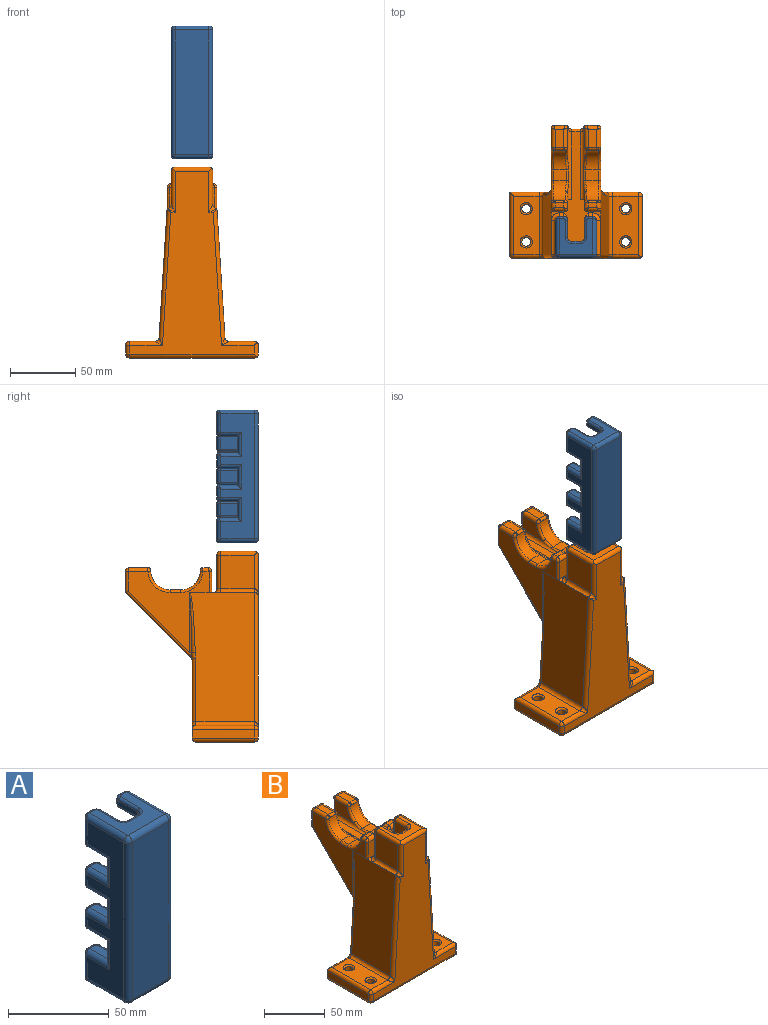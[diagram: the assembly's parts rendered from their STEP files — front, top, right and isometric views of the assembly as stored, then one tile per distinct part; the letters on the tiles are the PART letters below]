
ASSEMBLY  parts=2 mates=1
PART A: 197 faces, bbox 31.8x31.8x101.6 mm
  f0: plane 13.05x3.15mm, normal (-1,0,0), area 41.1mm2, adj f21,f33,f89,f134
  f1: plane 13.05x9.5mm, normal (-1,0,0), area 124mm2, adj f22,f33,f85,f98
  f2: plane 13.05x9.5mm, normal (-1,0,0), area 124mm2, adj f23,f33,f94,f107
  f3: plane 13.05x9.5mm, normal (-1,0,0), area 124mm2, adj f24,f33,f103,f116
  f4: plane 15.85x13.05mm, normal (1,0,0), area 206.8mm2, adj f31,f34,f62,f130
  f5: plane 13.05x9.1mm, normal (1,0,0), area 118.8mm2, adj f13,f34,f71,f76
  f6: plane 16.65x13.05mm, normal (1,0,0), area 217.3mm2, adj f14,f34,f80,f121
  f7: plane 9.1x3.53mm, normal (0,1,0), area 32.1mm2, adj f12,f56,f65,f194
  f8: plane 9.1x3.53mm, normal (0,1,0), area 32.1mm2, adj f13,f73,f74,f187
  f9: plane 16.65x3.53mm, normal (0,1,0), area 58.7mm2, adj f14,f82,f119,f140
  f10: plane 13.05x9.1mm, normal (1,0,0), area 118.8mm2, adj f12,f34,f59,f67
  f11: plane 95.6x25.75mm, normal (-1,0,0), area 1571.1mm2, adj f137,f139,f140,f145,f146,f151,f152,f184
  f12: cylinder r=3mm len=9.1mm, axis (0,0,1), area 42.9mm2, adj f7,f10,f57,f66
  f13: cylinder r=3mm len=9.1mm, axis (0,0,1), area 42.9mm2, adj f5,f8,f72,f75
  f14: cylinder r=3mm len=16.65mm, axis (0,0,1), area 78.5mm2, adj f6,f9,f81,f120
  f15: plane 3.53x3.15mm, normal (0,1,0), area 11.1mm2, adj f21,f91,f136,f162
  f16: plane 9.5x3.53mm, normal (0,1,0), area 33.5mm2, adj f22,f83,f100,f182
  f17: plane 9.5x3.53mm, normal (0,1,0), area 33.5mm2, adj f23,f92,f109,f174
  f18: plane 9.5x3.53mm, normal (0,1,0), area 33.5mm2, adj f24,f101,f118,f168
  f19: plane 95.6x25.75mm, normal (1,0,0), area 1274.2mm2, adj f141,f147,f154,f158,f160,f162,f164,f165
  f20: plane 13.05x3.15mm, normal (-1,0,0), area 41.1mm2, adj f32,f33,f112,f125
  f21: cylinder r=3mm len=3.15mm, axis (0,0,-1), area 14.8mm2, adj f0,f15,f90,f135
  f22: cylinder r=3mm len=9.5mm, axis (0,0,-1), area 44.8mm2, adj f1,f16,f84,f99
  f23: cylinder r=3mm len=9.5mm, axis (0,0,-1), area 44.8mm2, adj f2,f17,f93,f108
  f24: cylinder r=3mm len=9.5mm, axis (0,0,-1), area 44.8mm2, adj f3,f18,f102,f117
  f25: plane 15.85x3.53mm, normal (0,1,0), area 55.9mm2, adj f31,f64,f128,f145
  f26: plane 95.6x25.75mm, normal (0,-1,0), area 2461.7mm2, adj f152,f153,f157,f158
  f27: plane 3.53x3.15mm, normal (0,1,0), area 11.1mm2, adj f32,f110,f127,f147
  f28: plane 98.4x6.7mm, normal (0,1,0), area 659.3mm2, adj f33,f34,f123,f132
  f29: plane 27.15x25.75mm, normal (0,0,1), area 404.5mm2, adj f119,f120,f121,f122,f123,f124,f125,f126
  f30: plane 27.15x25.75mm, normal (0,0,-1), area 404.5mm2, adj f128,f129,f130,f131,f132,f133,f134,f135
  f31: cylinder r=3mm len=15.85mm, axis (0,0,1), area 74.7mm2, adj f4,f25,f63,f129
  f32: cylinder r=3mm len=3.15mm, axis (0,0,-1), area 14.8mm2, adj f20,f27,f111,f126
  f33: cylinder r=3mm len=98.4mm, axis (0,0,-1), area 403.6mm2, adj f0,f1,f2,f3,f20,f28,f86,f87
  f34: cylinder r=3mm len=98.4mm, axis (0,0,1), area 418.6mm2, adj f4,f5,f6,f10,f28,f58,f60,f61
  f35: plane 12.73x5.15mm, normal (0,1,0), area 65.4mm2, adj f36,f37,f112,f114,f116,f165
  f36: plane 14.28x4.93mm, normal (0,0,1), area 69.9mm2, adj f35,f116,f117,f118,f166
  f37: plane 14.28x4.93mm, normal (0,0,-1), area 69.9mm2, adj f35,f110,f111,f112,f141
  f38: plane 12.73x5.15mm, normal (0,1,0), area 65.4mm2, adj f39,f40,f103,f105,f107,f171
  f39: plane 14.28x4.93mm, normal (0,0,1), area 69.9mm2, adj f38,f107,f108,f109,f172
  f40: plane 14.28x4.93mm, normal (0,0,-1), area 69.9mm2, adj f38,f101,f102,f103,f170
  f41: plane 12.73x5.15mm, normal (0,1,0), area 65.4mm2, adj f42,f43,f94,f96,f98,f177
  f42: plane 14.28x4.93mm, normal (0,0,1), area 69.9mm2, adj f41,f98,f99,f100,f178
  f43: plane 14.28x4.93mm, normal (0,0,-1), area 69.9mm2, adj f41,f92,f93,f94,f176
  f44: plane 12.73x5.15mm, normal (0,1,0), area 65.4mm2, adj f45,f46,f85,f87,f89,f179
  f45: plane 14.28x4.93mm, normal (0,0,1), area 69.9mm2, adj f44,f89,f90,f91,f164
  f46: plane 14.28x4.93mm, normal (0,0,-1), area 69.9mm2, adj f44,f83,f84,f85,f181
  f47: plane 12.73x5.15mm, normal (0,1,0), area 65.4mm2, adj f48,f49,f76,f78,f80,f184
  f48: plane 14.28x4.93mm, normal (0,0,-1), area 69.9mm2, adj f47,f80,f81,f82,f137
  f49: plane 14.28x4.93mm, normal (0,0,1), area 69.9mm2, adj f47,f74,f75,f76,f185
  f50: plane 12.73x5.15mm, normal (0,1,0), area 65.4mm2, adj f51,f52,f67,f69,f71,f190
  f51: plane 14.28x4.93mm, normal (0,0,-1), area 69.9mm2, adj f50,f71,f72,f73,f189
  f52: plane 14.28x4.93mm, normal (0,0,1), area 69.9mm2, adj f50,f65,f66,f67,f191
  f53: plane 12.73x5.15mm, normal (0,1,0), area 65.4mm2, adj f54,f55,f59,f61,f62,f193
  f54: plane 14.28x4.93mm, normal (0,0,1), area 69.9mm2, adj f53,f62,f63,f64,f139
  f55: plane 14.28x4.93mm, normal (0,0,-1), area 69.9mm2, adj f53,f56,f57,f59,f195
  f56: cylinder r=1.6mm len=3.53mm, axis (-1,0,0), area 8.9mm2, adj f7,f55,f57,f196
  f57: torus R=1.4mm, axis (0,0,-1), area 9.5mm2, adj f12,f55,f56,f59
  f58: torus R=4.6mm, axis (0,0,-1), area 0.6mm2, adj f34,f59,f61
  f59: cylinder r=1.6mm len=13.05mm, axis (0,1,0), area 32.7mm2, adj f10,f53,f55,f57,f58,f61
  f60: torus R=4.6mm, axis (0,0,-1), area 0.6mm2, adj f34,f61,f62
  f61: cylinder r=1.6mm len=15.9mm, axis (0,0,1), area 28mm2, adj f34,f53,f58,f59,f60,f62
  f62: cylinder r=1.6mm len=13.05mm, axis (0,-1,0), area 32.7mm2, adj f4,f53,f54,f60,f61,f63
  f63: torus R=1.4mm, axis (0,0,-1), area 9.5mm2, adj f31,f54,f62,f64
  f64: cylinder r=1.6mm len=3.53mm, axis (1,0,0), area 8.9mm2, adj f25,f54,f63,f142
  f65: cylinder r=1.6mm len=3.53mm, axis (1,0,0), area 8.9mm2, adj f7,f52,f66,f192
  f66: torus R=1.4mm, axis (0,0,-1), area 9.5mm2, adj f12,f52,f65,f67
  f67: cylinder r=1.6mm len=13.05mm, axis (0,-1,0), area 32.7mm2, adj f10,f50,f52,f66,f68,f69
  f68: torus R=4.6mm, axis (0,0,-1), area 0.6mm2, adj f34,f67,f69
  f69: cylinder r=1.6mm len=15.9mm, axis (0,0,1), area 28mm2, adj f34,f50,f67,f68,f70,f71
  f70: torus R=4.6mm, axis (0,0,-1), area 0.6mm2, adj f34,f69,f71
  f71: cylinder r=1.6mm len=13.05mm, axis (0,1,0), area 32.7mm2, adj f5,f50,f51,f69,f70,f72
  f72: torus R=1.4mm, axis (0,0,-1), area 9.5mm2, adj f13,f51,f71,f73
  f73: cylinder r=1.6mm len=3.53mm, axis (-1,0,0), area 8.9mm2, adj f8,f51,f72,f188
  f74: cylinder r=1.6mm len=3.53mm, axis (1,0,0), area 8.9mm2, adj f8,f49,f75,f186
  f75: torus R=1.4mm, axis (0,0,-1), area 9.5mm2, adj f13,f49,f74,f76
  f76: cylinder r=1.6mm len=13.05mm, axis (0,-1,0), area 32.7mm2, adj f5,f47,f49,f75,f77,f78
  f77: torus R=4.6mm, axis (0,0,-1), area 0.6mm2, adj f34,f76,f78
  f78: cylinder r=1.6mm len=15.9mm, axis (0,0,1), area 28mm2, adj f34,f47,f76,f77,f79,f80
  f79: torus R=4.6mm, axis (0,0,-1), area 0.6mm2, adj f34,f78,f80
  f80: cylinder r=1.6mm len=13.05mm, axis (0,1,0), area 32.7mm2, adj f6,f47,f48,f78,f79,f81
  f81: torus R=1.4mm, axis (0,0,-1), area 9.5mm2, adj f14,f48,f80,f82
  f82: cylinder r=1.6mm len=3.53mm, axis (-1,0,0), area 8.9mm2, adj f9,f48,f81,f138
  f83: cylinder r=1.6mm len=3.53mm, axis (-1,0,0), area 8.9mm2, adj f16,f46,f84,f183
  f84: torus R=1.4mm, axis (0,0,1), area 9.5mm2, adj f22,f46,f83,f85
  f85: cylinder r=1.6mm len=13.05mm, axis (0,-1,0), area 32.7mm2, adj f1,f44,f46,f84,f86,f87
  f86: torus R=4.6mm, axis (0,0,1), area 0.6mm2, adj f33,f85,f87
  f87: cylinder r=1.6mm len=15.9mm, axis (0,0,-1), area 28mm2, adj f33,f44,f85,f86,f88,f89
  f88: torus R=4.6mm, axis (0,0,1), area 0.6mm2, adj f33,f87,f89
  f89: cylinder r=1.6mm len=13.05mm, axis (0,1,0), area 32.7mm2, adj f0,f44,f45,f87,f88,f90
  f90: torus R=1.4mm, axis (0,0,1), area 9.5mm2, adj f21,f45,f89,f91
  f91: cylinder r=1.6mm len=3.53mm, axis (1,0,0), area 8.9mm2, adj f15,f45,f90,f163
  f92: cylinder r=1.6mm len=3.53mm, axis (-1,0,0), area 8.9mm2, adj f17,f43,f93,f175
  f93: torus R=1.4mm, axis (0,0,1), area 9.5mm2, adj f23,f43,f92,f94
  f94: cylinder r=1.6mm len=13.05mm, axis (0,-1,0), area 32.7mm2, adj f2,f41,f43,f93,f95,f96
  f95: torus R=4.6mm, axis (0,0,1), area 0.6mm2, adj f33,f94,f96
  f96: cylinder r=1.6mm len=15.9mm, axis (0,0,-1), area 28mm2, adj f33,f41,f94,f95,f97,f98
  f97: torus R=4.6mm, axis (0,0,1), area 0.6mm2, adj f33,f96,f98
  f98: cylinder r=1.6mm len=13.05mm, axis (0,1,0), area 32.7mm2, adj f1,f41,f42,f96,f97,f99
  f99: torus R=1.4mm, axis (0,0,1), area 9.5mm2, adj f22,f42,f98,f100
  f100: cylinder r=1.6mm len=3.53mm, axis (1,0,0), area 8.9mm2, adj f16,f42,f99,f180
  f101: cylinder r=1.6mm len=3.53mm, axis (-1,0,0), area 8.9mm2, adj f18,f40,f102,f169
  f102: torus R=1.4mm, axis (0,0,1), area 9.5mm2, adj f24,f40,f101,f103
  f103: cylinder r=1.6mm len=13.05mm, axis (0,-1,0), area 32.7mm2, adj f3,f38,f40,f102,f104,f105
  f104: torus R=4.6mm, axis (0,0,1), area 0.6mm2, adj f33,f103,f105
  f105: cylinder r=1.6mm len=15.9mm, axis (0,0,-1), area 28mm2, adj f33,f38,f103,f104,f106,f107
  f106: torus R=4.6mm, axis (0,0,1), area 0.6mm2, adj f33,f105,f107
  f107: cylinder r=1.6mm len=13.05mm, axis (0,1,0), area 32.7mm2, adj f2,f38,f39,f105,f106,f108
  f108: torus R=1.4mm, axis (0,0,1), area 9.5mm2, adj f23,f39,f107,f109
  f109: cylinder r=1.6mm len=3.53mm, axis (1,0,0), area 8.9mm2, adj f17,f39,f108,f173
  f110: cylinder r=1.6mm len=3.53mm, axis (-1,0,0), area 8.9mm2, adj f27,f37,f111,f144
  f111: torus R=1.4mm, axis (0,0,1), area 9.5mm2, adj f32,f37,f110,f112
  f112: cylinder r=1.6mm len=13.05mm, axis (0,-1,0), area 32.7mm2, adj f20,f35,f37,f111,f113,f114
  f113: torus R=4.6mm, axis (0,0,1), area 0.6mm2, adj f33,f112,f114
  f114: cylinder r=1.6mm len=15.9mm, axis (0,0,-1), area 28mm2, adj f33,f35,f112,f113,f115,f116
  f115: torus R=4.6mm, axis (0,0,1), area 0.6mm2, adj f33,f114,f116
  f116: cylinder r=1.6mm len=13.05mm, axis (0,1,0), area 32.7mm2, adj f3,f35,f36,f114,f115,f117
  f117: torus R=1.4mm, axis (0,0,1), area 9.5mm2, adj f24,f36,f116,f118
  f118: cylinder r=1.6mm len=3.53mm, axis (1,0,0), area 8.9mm2, adj f18,f36,f117,f167
  f119: cylinder r=1.6mm len=3.53mm, axis (1,0,0), area 8.9mm2, adj f9,f29,f120,f143
  f120: torus R=1.4mm, axis (0,0,1), area 9.5mm2, adj f14,f29,f119,f121
  f121: cylinder r=1.6mm len=13.05mm, axis (0,-1,0), area 32.8mm2, adj f6,f29,f120,f122
  f122: torus R=4.6mm, axis (0,0,1), area 14.1mm2, adj f29,f34,f121,f123
  f123: cylinder r=1.6mm len=6.7mm, axis (1,0,0), area 16.8mm2, adj f28,f29,f122,f124
  f124: torus R=4.6mm, axis (0,0,1), area 14.1mm2, adj f29,f33,f123,f125
  f125: cylinder r=1.6mm len=13.05mm, axis (0,1,0), area 32.8mm2, adj f20,f29,f124,f126
  f126: torus R=1.4mm, axis (0,0,1), area 9.5mm2, adj f29,f32,f125,f127
  f127: cylinder r=1.6mm len=3.53mm, axis (1,0,0), area 8.9mm2, adj f27,f29,f126,f150
  f128: cylinder r=1.6mm len=3.53mm, axis (-1,0,0), area 8.9mm2, adj f25,f30,f129,f148
  f129: torus R=1.4mm, axis (0,0,1), area 9.5mm2, adj f30,f31,f128,f130
  f130: cylinder r=1.6mm len=13.05mm, axis (0,1,0), area 32.8mm2, adj f4,f30,f129,f131
  f131: torus R=4.6mm, axis (0,0,1), area 14.1mm2, adj f30,f34,f130,f132
  f132: cylinder r=1.6mm len=6.7mm, axis (-1,0,0), area 16.8mm2, adj f28,f30,f131,f133
  f133: torus R=4.6mm, axis (0,0,1), area 14.1mm2, adj f30,f33,f132,f134
  f134: cylinder r=1.6mm len=13.05mm, axis (0,-1,0), area 32.8mm2, adj f0,f30,f133,f135
  f135: torus R=1.4mm, axis (0,0,1), area 9.5mm2, adj f21,f30,f134,f136
  f136: cylinder r=1.6mm len=3.53mm, axis (-1,0,0), area 8.9mm2, adj f15,f30,f135,f161
  f137: cylinder r=3mm len=17.28mm, axis (0,1,0), area 70mm2, adj f11,f48,f138,f184
  f138: bspline ~3.6x3mm, area 7.9mm2, adj f82,f137,f140
  f139: cylinder r=3mm len=17.28mm, axis (0,-1,0), area 70mm2, adj f11,f54,f142,f193
  f140: cylinder r=3mm len=16.65mm, axis (0,0,1), area 73.7mm2, adj f9,f11,f138,f143
  f141: cylinder r=3mm len=17.28mm, axis (0,-1,0), area 70mm2, adj f19,f37,f144,f165
  f142: bspline ~3.6x3mm, area 7.9mm2, adj f64,f139,f145
  f143: bspline ~3.6x3mm, area 7.9mm2, adj f119,f140,f146
  f144: bspline ~3.6x3mm, area 7.9mm2, adj f110,f141,f147
  f145: cylinder r=3mm len=15.85mm, axis (0,0,1), area 69.9mm2, adj f11,f25,f142,f148
  f146: cylinder r=3mm len=27.15mm, axis (0,1,0), area 125.5mm2, adj f11,f29,f143,f149
  f147: cylinder r=3mm len=3.15mm, axis (0,0,-1), area 10mm2, adj f19,f27,f144,f150
  f148: bspline ~3.15x3mm, area 7.8mm2, adj f128,f145,f151
  f149: sphere r=3mm, area 14.1mm2, adj f146,f152,f153
  f150: bspline ~3.15x3mm, area 7.8mm2, adj f127,f147,f154
  f151: cylinder r=3mm len=27.15mm, axis (0,-1,0), area 125.5mm2, adj f11,f30,f148,f155
  f152: cylinder r=3mm len=95.6mm, axis (0,0,-1), area 450.5mm2, adj f11,f26,f149,f155
  f153: cylinder r=3mm len=25.75mm, axis (-1,0,0), area 121.3mm2, adj f26,f29,f149,f156
  f154: cylinder r=3mm len=27.15mm, axis (0,-1,0), area 125.5mm2, adj f19,f29,f150,f156
  f155: sphere r=3mm, area 14.1mm2, adj f151,f152,f157
  f156: sphere r=3mm, area 14.1mm2, adj f153,f154,f158
  f157: cylinder r=3mm len=25.75mm, axis (1,0,0), area 121.3mm2, adj f26,f30,f155,f159
  f158: cylinder r=3mm len=95.6mm, axis (0,0,1), area 450.5mm2, adj f19,f26,f156,f159
  f159: sphere r=3mm, area 14.1mm2, adj f157,f158,f160
  f160: cylinder r=3mm len=27.15mm, axis (0,1,0), area 125.5mm2, adj f19,f30,f159,f161
  f161: bspline ~3.6x3mm, area 7.9mm2, adj f136,f160,f162
  f162: cylinder r=3mm len=3.15mm, axis (0,0,-1), area 10mm2, adj f15,f19,f161,f163
  f163: bspline ~3.6x3mm, area 7.9mm2, adj f91,f162,f164
  f164: cylinder r=3mm len=17.28mm, axis (0,1,0), area 70mm2, adj f19,f45,f163,f179
  f165: cylinder r=3mm len=18.7mm, axis (0,0,-1), area 70.1mm2, adj f19,f35,f141,f166
  f166: cylinder r=3mm len=17.28mm, axis (0,1,0), area 70mm2, adj f19,f36,f165,f167
  f167: bspline ~3.6x3mm, area 7.9mm2, adj f118,f166,f168
  f168: cylinder r=3mm len=9.5mm, axis (0,0,-1), area 40mm2, adj f18,f19,f167,f169
  f169: bspline ~3.6x3mm, area 7.9mm2, adj f101,f168,f170
  f170: cylinder r=3mm len=17.28mm, axis (0,-1,0), area 70mm2, adj f19,f40,f169,f171
  f171: cylinder r=3mm len=18.7mm, axis (0,0,-1), area 70.1mm2, adj f19,f38,f170,f172
  f172: cylinder r=3mm len=17.28mm, axis (0,1,0), area 70mm2, adj f19,f39,f171,f173
  f173: bspline ~3.6x3mm, area 7.9mm2, adj f109,f172,f174
  f174: cylinder r=3mm len=9.5mm, axis (0,0,-1), area 40mm2, adj f17,f19,f173,f175
  f175: bspline ~3.6x3mm, area 7.9mm2, adj f92,f174,f176
  f176: cylinder r=3mm len=17.28mm, axis (0,-1,0), area 70mm2, adj f19,f43,f175,f177
  f177: cylinder r=3mm len=18.7mm, axis (0,0,-1), area 70.1mm2, adj f19,f41,f176,f178
  f178: cylinder r=3mm len=17.28mm, axis (0,1,0), area 70mm2, adj f19,f42,f177,f180
  f179: cylinder r=3mm len=18.7mm, axis (0,0,-1), area 70.1mm2, adj f19,f44,f164,f181
  f180: bspline ~3.6x3mm, area 7.9mm2, adj f100,f178,f182
  f181: cylinder r=3mm len=17.28mm, axis (0,-1,0), area 70mm2, adj f19,f46,f179,f183
  f182: cylinder r=3mm len=9.5mm, axis (0,0,-1), area 40mm2, adj f16,f19,f180,f183
  f183: bspline ~3.6x3mm, area 7.9mm2, adj f83,f181,f182
  f184: cylinder r=3mm len=18.7mm, axis (0,0,1), area 70.1mm2, adj f11,f47,f137,f185
  f185: cylinder r=3mm len=17.28mm, axis (0,-1,0), area 70mm2, adj f11,f49,f184,f186
  f186: bspline ~3.6x3mm, area 7.9mm2, adj f74,f185,f187
  f187: cylinder r=3mm len=9.1mm, axis (0,0,1), area 38.1mm2, adj f8,f11,f186,f188
  f188: bspline ~3.6x3mm, area 7.9mm2, adj f73,f187,f189
  f189: cylinder r=3mm len=17.28mm, axis (0,1,0), area 70mm2, adj f11,f51,f188,f190
  f190: cylinder r=3mm len=18.7mm, axis (0,0,1), area 70.1mm2, adj f11,f50,f189,f191
  f191: cylinder r=3mm len=17.28mm, axis (0,-1,0), area 70mm2, adj f11,f52,f190,f192
  f192: bspline ~3.6x3mm, area 7.9mm2, adj f65,f191,f194
  f193: cylinder r=3mm len=18.7mm, axis (0,0,1), area 70.1mm2, adj f11,f53,f139,f195
  f194: cylinder r=3mm len=9.1mm, axis (0,0,1), area 38.1mm2, adj f7,f11,f192,f196
  f195: cylinder r=3mm len=17.28mm, axis (0,1,0), area 70mm2, adj f11,f55,f193,f196
  f196: bspline ~3.6x3mm, area 7.9mm2, adj f56,f194,f195
PART B: 200 faces, bbox 102.7x102.7x147.2 mm
  f0: plane 62.07x61.9mm, normal (1,0,0), area 1497.4mm2, adj f9,f28,f75,f94,f102,f104,f105,f155
  f1: plane 62.07x61.9mm, normal (-1,0,0), area 1497.4mm2, adj f7,f29,f69,f97,f98,f99,f118,f140
  f2: plane 16.05x12.06mm, normal (1,0,0), area 113.2mm2, adj f6,f16,f66,f77,f120,f135
  f3: plane 6.7x3.7mm, normal (0,0,1), area 24.8mm2, adj f6,f7,f67,f134
  f4: plane 16.05x12.06mm, normal (-1,0,0), area 113.2mm2, adj f8,f16,f71,f76,f116,f156
  f5: plane 6.7x3.7mm, normal (0,0,1), area 24.8mm2, adj f8,f9,f73,f150
  f6: cylinder r=3mm len=4.73mm, axis (0,-1,0), area 19.8mm2, adj f2,f3,f121,f132,f133
  f7: cylinder r=3mm len=4.73mm, axis (0,-1,0), area 19.8mm2, adj f1,f3,f119,f136,f138
  f8: cylinder r=3mm len=4.73mm, axis (0,1,0), area 19.8mm2, adj f4,f5,f117,f152,f154
  f9: cylinder r=3mm len=4.73mm, axis (0,-1,0), area 19.8mm2, adj f0,f5,f95,f151,f153
  f10: plane 25.75x3.53mm, normal (0,1,0), area 90.8mm2, adj f13,f14,f57,f84
  f11: plane 25.75x25.75mm, normal (0,0,1), area 322.3mm2, adj f14,f47,f56,f62,f65,f88,f89,f91
  f12: plane 16.05x8.7mm, normal (0,-1,0), area 139.6mm2, adj f16,f67,f118,f120
  f13: cylinder r=3mm len=3.53mm, axis (-1,0,0), area 16.6mm2, adj f10,f16,f54,f82
  f14: cylinder r=3mm len=3.53mm, axis (1,0,0), area 16.6mm2, adj f10,f11,f60,f86
  f15: plane 16.05x9.59mm, normal (0,1,0), area 140.6mm2, adj f39,f74,f105,f112,f113,f114
  f16: plane 94.89x39.22mm, normal (0,0,1), area 818.2mm2, adj f2,f4,f12,f13,f28,f29,f36,f43
  f17: plane 44.8x19.58mm, normal (0,0,1), area 738.3mm2, adj f48,f173,f175,f178,f179,f180
  f18: plane 140.05x95.6mm, normal (0,-1,0), area 5401.5mm2, adj f40,f41,f42,f43,f44,f45,f46,f47
  f19: plane 44.8x6.7mm, normal (1,0,0), area 300.2mm2, adj f42,f188,f190,f191
  f20: plane 98.6x60.57mm, normal (0,1,0), area 2892.3mm2, adj f21,f100,f101,f103,f180,f181,f182,f187
  f21: plane 47.8x6.7mm, normal (-1,0,0), area 320.3mm2, adj f20,f46,f178,f186
  f22: plane 44.8x19.58mm, normal (0,0,1), area 738.3mm2, adj f40,f169,f171,f191,f194,f195
  f23: plane 95.6x44.8mm, normal (0,0,-1), area 4005.1mm2, adj f44,f168,f170,f172,f174,f186,f187,f188
  f24: cylinder r=3.3mm len=9.9mm, axis (0,0,1), area 205.4mm2, adj f174,f175
  f25: cylinder r=3.3mm len=9.9mm, axis (0,0,1), area 205.4mm2, adj f172,f173
  f26: cylinder r=3.3mm len=9.9mm, axis (0,0,1), area 205.4mm2, adj f170,f171
  f27: cylinder r=3.3mm len=9.9mm, axis (0,0,1), area 205.4mm2, adj f168,f169
  f28: plane 98.79x49.56mm, normal (1,0,0.06), area 4515.6mm2, adj f0,f16,f41,f195,f197,f198,f199
  f29: plane 98.79x49.56mm, normal (-1,0,0.06), area 4515.6mm2, adj f1,f16,f50,f179,f182,f183,f184
  f30: plane 25.75x25.75mm, normal (-1,0,0), area 663.1mm2, adj f49,f53,f56,f57
  f31: plane 25.75x25.75mm, normal (1,0,0), area 663.1mm2, adj f45,f59,f63,f65
  f32: plane 25.75x3.53mm, normal (0,1,0), area 90.8mm2, adj f58,f62,f63,f83
  f33: plane 16.05x9.59mm, normal (0,1,0), area 140.6mm2, adj f39,f70,f97,f108,f109,f110
  f34: plane 22.41x13.05mm, normal (1,0,0), area 227.1mm2, adj f66,f68,f108,f143
  f35: plane 14.05x6.7mm, normal (0,0,1), area 94.1mm2, adj f68,f69,f70,f149
  f36: plane 16.05x8.7mm, normal (0,-1,0), area 139.6mm2, adj f16,f73,f94,f116
  f37: plane 22.41x13.05mm, normal (-1,0,0), area 227.1mm2, adj f71,f72,f114,f164
  f38: plane 14.05x6.7mm, normal (0,0,1), area 94.1mm2, adj f72,f74,f75,f165
  f39: plane 50.21x50.21mm, normal (0,0.71,-0.71), area 2355.7mm2, adj f15,f33,f98,f101,f104,f110,f111,f112
  f40: cylinder r=3mm len=27.34mm, axis (-1,0,0), area 110.6mm2, adj f18,f22,f42,f191,f193
  f41: cylinder r=3mm len=104.6mm, axis (-0.06,0,1), area 473.1mm2, adj f18,f28,f43,f193
  f42: cylinder r=3mm len=10.94mm, axis (0,0,1), area 41.6mm2, adj f18,f19,f40,f44,f188,f191
  f43: cylinder r=3mm len=6.18mm, axis (-1,0,0), area 6.3mm2, adj f16,f18,f41,f55
  f44: cylinder r=3mm len=97.72mm, axis (1,0,0), area 455.5mm2, adj f18,f23,f42,f185,f188
  f45: cylinder r=3mm len=33.87mm, axis (0,0,1), area 140.5mm2, adj f18,f31,f47,f55,f65
  f46: cylinder r=3mm len=6.7mm, axis (0,0,-1), area 31.6mm2, adj f18,f21,f176,f185
  f47: cylinder r=3mm len=29.99mm, axis (-1,0,0), area 131.3mm2, adj f11,f18,f45,f49,f56,f65
  f48: cylinder r=3mm len=25.22mm, axis (-1,0,0), area 105.6mm2, adj f17,f18,f176,f177
  f49: cylinder r=3mm len=33.87mm, axis (0,0,-1), area 140.5mm2, adj f18,f30,f47,f52,f56
  f50: cylinder r=3mm len=104.6mm, axis (0.06,0,1), area 473.1mm2, adj f18,f29,f51,f177
  f51: cylinder r=3mm len=6.18mm, axis (-1,0,0), area 6.3mm2, adj f16,f18,f50,f52
  f52: bspline ~6x6mm, area 9.5mm2, adj f49,f51,f53
  f53: cylinder r=3mm len=25.75mm, axis (0,-1,0), area 121.3mm2, adj f16,f30,f52,f54
  f54: torus R=6mm, axis (0,0,1), area 30.3mm2, adj f13,f16,f53,f57
  f55: bspline ~6x6mm, area 9.5mm2, adj f43,f45,f59
  f56: cylinder r=3mm len=27.87mm, axis (0,1,0), area 126.3mm2, adj f11,f30,f47,f49,f60
  f57: cylinder r=3mm len=25.75mm, axis (0,0,-1), area 121.3mm2, adj f10,f30,f54,f60
  f58: cylinder r=3mm len=3.53mm, axis (-1,0,0), area 16.6mm2, adj f16,f32,f61,f81
  f59: cylinder r=3mm len=25.75mm, axis (0,1,0), area 121.3mm2, adj f16,f31,f55,f61
  f60: sphere r=3mm, area 14.1mm2, adj f14,f56,f57
  f61: torus R=6mm, axis (0,0,1), area 30.3mm2, adj f16,f58,f59,f63
  f62: cylinder r=3mm len=3.53mm, axis (1,0,0), area 16.6mm2, adj f11,f32,f64,f85
  f63: cylinder r=3mm len=25.75mm, axis (0,0,1), area 121.3mm2, adj f31,f32,f61,f64
  f64: sphere r=3mm, area 14.1mm2, adj f62,f63,f65
  f65: cylinder r=3mm len=27.87mm, axis (0,-1,0), area 126.3mm2, adj f11,f31,f45,f47,f64
  f66: cylinder r=3mm len=54.8mm, axis (0,1,0), area 219.2mm2, adj f2,f16,f34,f77,f109,f110,f137,f139
  f67: cylinder r=3mm len=8.7mm, axis (-1,0,0), area 36.3mm2, adj f3,f12,f119,f121
  f68: cylinder r=3mm len=15.08mm, axis (0,-1,0), area 68.6mm2, adj f34,f35,f107,f145,f147
  f69: cylinder r=3mm len=15.08mm, axis (0,-1,0), area 68.6mm2, adj f1,f35,f96,f146,f148
  f70: cylinder r=3mm len=8.7mm, axis (-1,0,0), area 36.3mm2, adj f33,f35,f96,f107
  f71: cylinder r=3mm len=54.8mm, axis (0,-1,0), area 219.2mm2, adj f4,f16,f37,f76,f112,f113,f158,f160
  f72: cylinder r=3mm len=15.08mm, axis (0,1,0), area 68.6mm2, adj f37,f38,f115,f166,f167
  f73: cylinder r=3mm len=8.7mm, axis (-1,0,0), area 36.3mm2, adj f5,f36,f95,f117
  f74: cylinder r=3mm len=8.7mm, axis (-1,0,0), area 36.3mm2, adj f15,f38,f106,f115
  f75: cylinder r=3mm len=15.08mm, axis (0,-1,0), area 68.6mm2, adj f0,f38,f106,f161,f163
  f76: plane 3x3mm, normal (0,-1,0), area 1.9mm2, adj f4,f16,f71
  f77: plane 3x3mm, normal (0,-1,0), area 1.9mm2, adj f2,f16,f66
  f78: plane 28.75x13.85mm, normal (1,0,0), area 376mm2, adj f16,f82,f84,f89,f90
  f79: plane 28.75x13.85mm, normal (-1,0,0), area 376mm2, adj f16,f81,f83,f87,f88
  f80: plane 28.75x6.7mm, normal (0,1,0), area 192.6mm2, adj f16,f87,f90,f93
  f81: torus R=6mm, axis (1,0,0), area 18.9mm2, adj f16,f58,f79,f83
  f82: torus R=6mm, axis (1,0,0), area 18.9mm2, adj f13,f16,f78,f84
  f83: cylinder r=3mm len=25.75mm, axis (0,0,1), area 121.3mm2, adj f32,f79,f81,f85
  f84: cylinder r=3mm len=25.75mm, axis (0,0,-1), area 121.3mm2, adj f10,f78,f82,f86
  f85: sphere r=3mm, area 9mm2, adj f62,f83,f88
  f86: sphere r=3mm, area 9mm2, adj f14,f84,f89
  f87: cylinder r=3mm len=28.75mm, axis (0,0,1), area 135.5mm2, adj f16,f79,f80,f91
  f88: cylinder r=3mm len=13.05mm, axis (0,-1,0), area 61.5mm2, adj f11,f79,f85,f91
  f89: cylinder r=3mm len=13.05mm, axis (0,1,0), area 61.5mm2, adj f11,f78,f86,f92
  f90: cylinder r=3mm len=28.75mm, axis (0,0,-1), area 135.5mm2, adj f16,f78,f80,f92
  f91: torus R=6mm, axis (0,0,1), area 30.3mm2, adj f11,f87,f88,f93
  f92: torus R=6mm, axis (0,0,1), area 30.3mm2, adj f11,f89,f90,f93
  f93: cylinder r=3mm len=6.7mm, axis (-1,0,0), area 31.6mm2, adj f11,f80,f91,f92
  f94: cylinder r=2mm len=16.05mm, axis (0,0,1), area 50.4mm2, adj f0,f16,f36,f95
  f95: bspline ~3.16x3mm, area 6.5mm2, adj f9,f73,f94
  f96: bspline ~3.65x3mm, area 6.5mm2, adj f69,f70,f97
  f97: cylinder r=2mm len=16.05mm, axis (0,0,-1), area 49.1mm2, adj f1,f33,f96,f98
  f98: cylinder r=2mm len=51.63mm, axis (0,-0.71,-0.71), area 215.5mm2, adj f1,f39,f97,f100
  f99: cylinder r=2mm len=45.88mm, axis (0,0,-1), area 67.6mm2, adj f1,f100,f184
  f100: bspline ~5.66x4mm, area 12mm2, adj f20,f98,f99,f101,f183
  f101: cylinder r=2mm len=34.1mm, axis (1,0,0), area 53.6mm2, adj f20,f39,f100,f103
  f102: cylinder r=2mm len=45.88mm, axis (0,0,1), area 67.6mm2, adj f0,f103,f199
  f103: bspline ~5.66x4mm, area 12mm2, adj f20,f101,f102,f104,f198
  f104: cylinder r=2mm len=51.63mm, axis (0,-0.71,-0.71), area 215.5mm2, adj f0,f39,f103,f105
  f105: cylinder r=2mm len=16.05mm, axis (0,0,1), area 49.1mm2, adj f0,f15,f104,f106
  f106: bspline ~3.65x3mm, area 6.5mm2, adj f74,f75,f105
  f107: bspline ~3.16x3mm, area 6.5mm2, adj f68,f70,f108
  f108: cylinder r=2mm len=13.05mm, axis (0,0,1), area 41mm2, adj f33,f34,f107,f109
  f109: torus R=5mm, axis (0,1,0), area 6.8mm2, adj f33,f66,f108,f110
  f110: bspline ~5.46x4.86mm, area 22mm2, adj f33,f39,f66,f109,f111
  f111: cylinder r=2mm len=6.7mm, axis (-1,0,0), area 31.6mm2, adj f16,f39,f110,f112
  f112: bspline ~5.46x4.86mm, area 22mm2, adj f15,f39,f71,f111,f113
  f113: torus R=5mm, axis (0,1,0), area 6.8mm2, adj f15,f71,f112,f114
  f114: cylinder r=2mm len=13.05mm, axis (0,0,1), area 41mm2, adj f15,f37,f113,f115
  f115: bspline ~3.65x3mm, area 6.5mm2, adj f72,f74,f114
  f116: cylinder r=2mm len=16.05mm, axis (0,0,1), area 50.4mm2, adj f4,f16,f36,f117
  f117: bspline ~3.16x3mm, area 6.5mm2, adj f8,f73,f116
  f118: cylinder r=2mm len=16.05mm, axis (0,0,-1), area 50.4mm2, adj f1,f12,f16,f119
  f119: bspline ~3.65x3mm, area 6.5mm2, adj f7,f67,f118
  f120: cylinder r=2mm len=16.05mm, axis (0,0,1), area 50.4mm2, adj f2,f12,f16,f121
  f121: bspline ~3.16x3mm, area 6.5mm2, adj f6,f67,f120
  f122: plane 9.7x8.1mm, normal (0,0,1), area 78.6mm2, adj f130,f131,f139,f142
  f123: plane 7.32x0.05mm, normal (0,-1,0), area 0.4mm2, adj f131,f147,f148,f149
  f124: plane 7.32x0.05mm, normal (0,1,0), area 0.4mm2, adj f130,f132,f134,f136
  f125: plane 7.32x0.05mm, normal (0,1,0), area 0.4mm2, adj f129,f150,f151,f152
  f126: plane 7.32x0.05mm, normal (0,-1,0), area 0.4mm2, adj f128,f163,f165,f167
  f127: plane 9.7x8.1mm, normal (0,0,1), area 78.6mm2, adj f128,f129,f157,f160
  f128: cylinder r=15mm len=15mm, axis (-1,0,0), area 208.9mm2, adj f126,f127,f159,f161,f162,f164,f166
  f129: cylinder r=15mm len=15mm, axis (1,0,0), area 208.9mm2, adj f125,f127,f153,f154,f155,f156,f158
  f130: cylinder r=15mm len=15mm, axis (1,0,0), area 208.9mm2, adj f122,f124,f133,f135,f137,f138,f140
  f131: cylinder r=15mm len=15mm, axis (-1,0,0), area 208.9mm2, adj f122,f123,f141,f143,f144,f145,f146
  f132: torus R=1mm, axis (0,1,0), area 2.3mm2, adj f6,f124,f133,f134
  f133: bspline ~3.66x2.91mm, area 8.7mm2, adj f6,f130,f132,f135
  f134: cylinder r=2mm len=6.7mm, axis (-1,0,0), area 21mm2, adj f3,f124,f132,f136
  f135: torus R=17mm, axis (-1,0,0), area 45mm2, adj f2,f130,f133,f137
  f136: torus R=1mm, axis (0,1,0), area 2.3mm2, adj f7,f124,f134,f138
  f137: bspline ~12.09x4.01mm, area 21.7mm2, adj f66,f130,f135,f139
  f138: bspline ~3.66x2.91mm, area 8.7mm2, adj f7,f130,f136,f140
  f139: cylinder r=2mm len=8.1mm, axis (0,1,0), area 15mm2, adj f66,f122,f137,f141
  f140: torus R=17mm, axis (-1,0,0), area 74.8mm2, adj f1,f130,f138,f142
  f141: bspline ~11.59x3.67mm, area 21.7mm2, adj f66,f131,f139,f143
  f142: cylinder r=2mm len=8.1mm, axis (0,1,0), area 25.4mm2, adj f1,f122,f140,f144
  f143: torus R=17mm, axis (-1,0,0), area 45mm2, adj f34,f131,f141,f145
  f144: torus R=17mm, axis (-1,0,0), area 74.8mm2, adj f1,f131,f142,f146
  f145: bspline ~3.66x2.91mm, area 8.7mm2, adj f68,f131,f143,f147
  f146: bspline ~3.66x2.91mm, area 8.7mm2, adj f69,f131,f144,f148
  f147: torus R=1mm, axis (0,1,0), area 2.3mm2, adj f68,f123,f145,f149
  f148: torus R=1mm, axis (0,1,0), area 2.3mm2, adj f69,f123,f146,f149
  f149: cylinder r=2mm len=6.7mm, axis (1,0,0), area 21mm2, adj f35,f123,f147,f148
  f150: cylinder r=2mm len=6.7mm, axis (-1,0,0), area 21mm2, adj f5,f125,f151,f152
  f151: torus R=1mm, axis (0,1,0), area 2.3mm2, adj f9,f125,f150,f153
  f152: torus R=1mm, axis (0,1,0), area 2.3mm2, adj f8,f125,f150,f154
  f153: bspline ~3.66x2.91mm, area 8.7mm2, adj f9,f129,f151,f155
  f154: bspline ~3.66x2.91mm, area 8.7mm2, adj f8,f129,f152,f156
  f155: torus R=17mm, axis (-1,0,0), area 74.8mm2, adj f0,f129,f153,f157
  f156: torus R=17mm, axis (1,0,0), area 45mm2, adj f4,f129,f154,f158
  f157: cylinder r=2mm len=8.1mm, axis (0,-1,0), area 25.4mm2, adj f0,f127,f155,f159
  f158: bspline ~11.59x3.67mm, area 21.7mm2, adj f71,f129,f156,f160
  f159: torus R=17mm, axis (-1,0,0), area 74.8mm2, adj f0,f128,f157,f161
  f160: cylinder r=2mm len=8.1mm, axis (0,-1,0), area 15mm2, adj f71,f127,f158,f162
  f161: bspline ~3.66x2.91mm, area 8.7mm2, adj f75,f128,f159,f163
  f162: bspline ~12.09x4.01mm, area 21.7mm2, adj f71,f128,f160,f164
  f163: torus R=1mm, axis (0,1,0), area 2.3mm2, adj f75,f126,f161,f165
  f164: torus R=17mm, axis (1,0,0), area 45mm2, adj f37,f128,f162,f166
  f165: cylinder r=2mm len=6.7mm, axis (1,0,0), area 21mm2, adj f38,f126,f163,f167
  f166: bspline ~3.66x2.91mm, area 8.7mm2, adj f72,f128,f164,f167
  f167: torus R=1mm, axis (0,1,0), area 2.3mm2, adj f72,f126,f165,f166
  f168: torus R=4.7mm, axis (0,0,1), area 52.7mm2, adj f23,f27
  f169: torus R=4.7mm, axis (0,0,1), area 52.7mm2, adj f22,f27
  f170: torus R=4.7mm, axis (0,0,1), area 52.7mm2, adj f23,f26
  f171: torus R=4.7mm, axis (0,0,1), area 52.7mm2, adj f22,f26
  f172: torus R=4.7mm, axis (0,0,1), area 52.7mm2, adj f23,f25
  f173: torus R=4.7mm, axis (0,0,1), area 52.7mm2, adj f17,f25
  f174: torus R=4.7mm, axis (0,0,1), area 52.7mm2, adj f23,f24
  f175: torus R=4.7mm, axis (0,0,1), area 52.7mm2, adj f17,f24
  f176: sphere r=3mm, area 14.1mm2, adj f46,f48,f178
  f177: bspline ~5.81x5.64mm, area 9mm2, adj f48,f50,f179
  f178: cylinder r=3mm len=47.8mm, axis (0,1,0), area 218.2mm2, adj f17,f21,f176,f180
  f179: cylinder r=3mm len=44.8mm, axis (0,1,0), area 202.7mm2, adj f17,f29,f177,f181
  f180: cylinder r=3mm len=22.58mm, axis (1,0,0), area 99.3mm2, adj f17,f20,f178,f181
  f181: torus R=6mm, axis (0,-1,0), area 29.1mm2, adj f20,f179,f180,f182
  f182: cylinder r=3mm len=48.43mm, axis (0.06,0,1), area 227.8mm2, adj f20,f29,f181,f183
  f183: bspline ~6.22x3.38mm, area 18.4mm2, adj f29,f100,f182,f184
  f184: bspline ~49.68x4.77mm, area 102mm2, adj f1,f29,f99,f183
  f185: sphere r=3mm, area 14.1mm2, adj f44,f46,f186
  f186: cylinder r=3mm len=47.8mm, axis (0,-1,0), area 218.2mm2, adj f21,f23,f185,f187
  f187: cylinder r=3mm len=98.6mm, axis (-1,0,0), area 457.6mm2, adj f20,f23,f186,f189
  f188: cylinder r=3mm len=46.92mm, axis (0,1,0), area 216.1mm2, adj f19,f23,f42,f44,f189
  f189: sphere r=3mm, area 9mm2, adj f187,f188,f190
  f190: cylinder r=3mm len=6.7mm, axis (0,0,-1), area 31.6mm2, adj f19,f20,f189,f192
  f191: cylinder r=3mm len=46.92mm, axis (0,-1,0), area 216.1mm2, adj f19,f22,f40,f42,f192
  f192: sphere r=3mm, area 9mm2, adj f190,f191,f194
  f193: bspline ~5.81x5.64mm, area 9mm2, adj f40,f41,f195
  f194: cylinder r=3mm len=19.58mm, axis (1,0,0), area 92.3mm2, adj f20,f22,f192,f196
  f195: cylinder r=3mm len=44.8mm, axis (0,-1,0), area 202.7mm2, adj f22,f28,f193,f196
  f196: torus R=6mm, axis (0,-1,0), area 29.1mm2, adj f20,f194,f195,f197
  f197: cylinder r=3mm len=48.43mm, axis (-0.06,0,1), area 227.8mm2, adj f20,f28,f196,f198
  f198: bspline ~5.42x3.2mm, area 18.4mm2, adj f28,f103,f197,f199
  f199: bspline ~49.68x4.77mm, area 102mm2, adj f0,f28,f102,f198
PLACE A t=(-25.41,-7.64,230.45)mm
PLACE B t=(-25.41,1.88,78.05)mm
MATE parallel A.f152 <-> B.f11  axis (0,0,-1) through (-38.28,-20.52,230.45)mm
